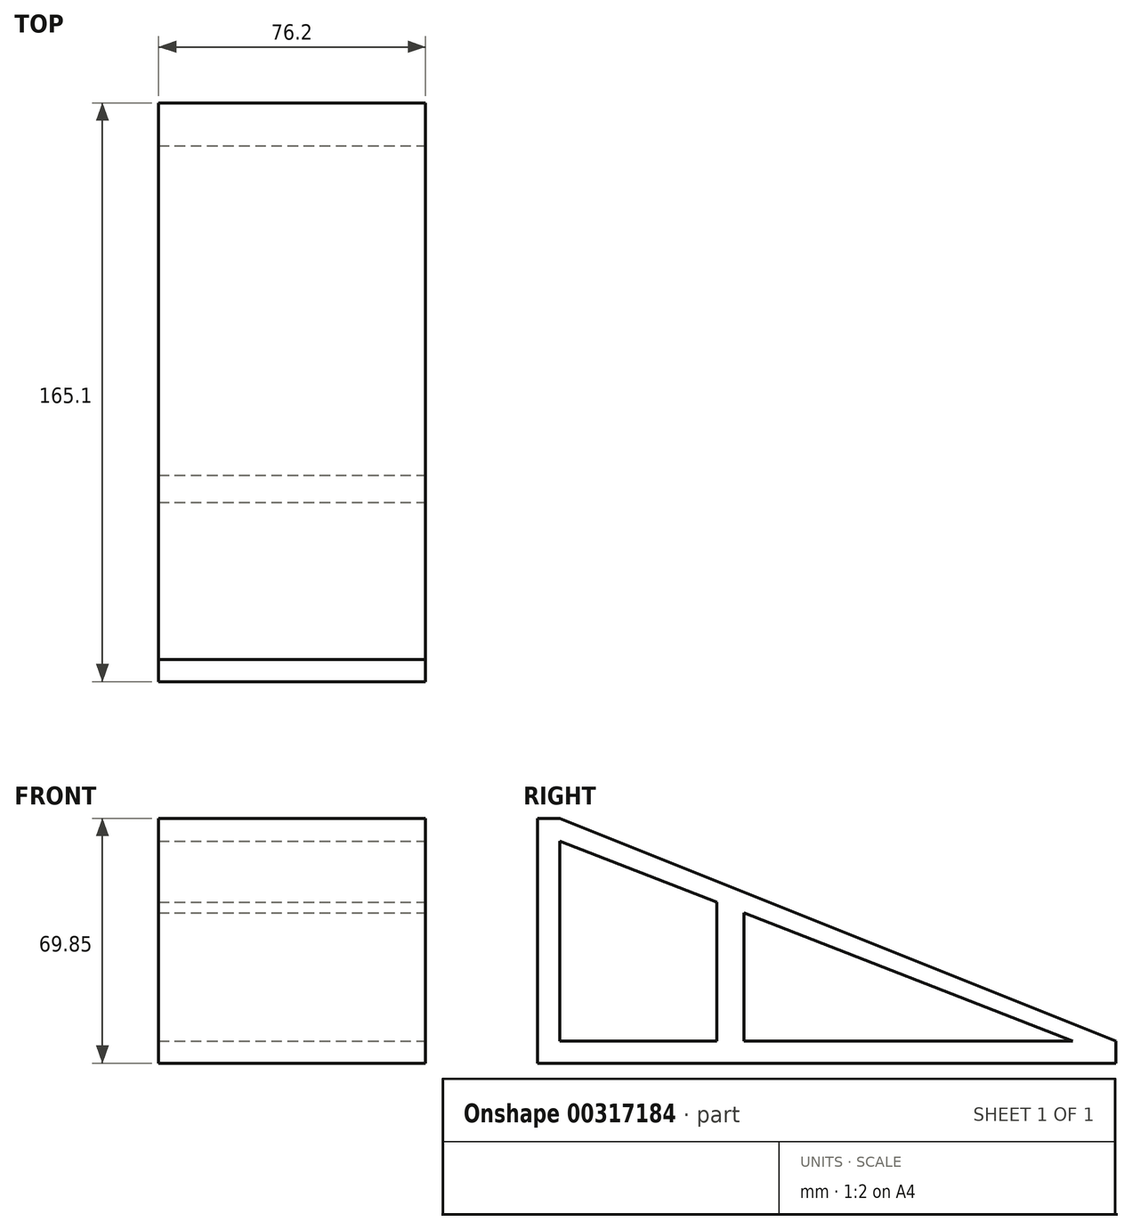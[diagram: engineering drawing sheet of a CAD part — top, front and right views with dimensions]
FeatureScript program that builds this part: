
annotation { "Feature Type Name" : "Feature", "Feature Type Description" : "" }
export const myFeature = defineFeature(function(context is Context, id is Id, definition is map)
    precondition{}
    {
        {
            var Q0;
            Q0=qCreatedBy(makeId("Right.planeOp"),FACE);
            var sketch = newSketch(context, id + "F0", { "sketchPlane" : qUnion([Q0])});
            skLineSegment(sketch, "E0.bottom", {"start": v(-82.55, 3.18) * mm, "end": v(82.55, 3.18) * mm});
            skLineSegment(sketch, "E0.top", {"start": v(-82.55, -3.18) * mm, "end": v(82.55, -3.18) * mm});
            skLineSegment(sketch, "E0.left", {"start": v(-82.55, 3.18) * mm, "end": v(-82.55, -3.18) * mm});
            skLineSegment(sketch, "E0.right", {"start": v(82.55, 3.18) * mm, "end": v(82.55, -3.18) * mm});
            skPoint(sketch, "E0.middle", {"position": v(0, 0) * mm});
            skLineSegment(sketch, "E1.bottom", {"start": v(-82.55, 3.18) * mm, "end": v(-76.2, 3.18) * mm});
            skLineSegment(sketch, "E1.top", {"start": v(-82.55, 66.68) * mm, "end": v(-76.2, 66.68) * mm});
            skLineSegment(sketch, "E1.left", {"start": v(-82.55, 3.18) * mm, "end": v(-82.55, 66.68) * mm});
            skLineSegment(sketch, "E1.right", {"start": v(-76.2, 3.18) * mm, "end": v(-76.2, 66.68) * mm});
            skLineSegment(sketch, "E2", {"start": v(-76.2, 66.68) * mm, "end": v(82.55, 3.18) * mm});
            skLineSegment(sketch, "E3", {"start": v(-76.2, 60.2) * mm, "end": v(70.25, 3.18) * mm});
            skLineSegment(sketch, "E4", {"start": v(-31.4, 3.18) * mm, "end": v(-31.4, 42.75) * mm});
            skLineSegment(sketch, "E5", {"start": v(-23.65, 3.18) * mm, "end": v(-23.65, 39.73) * mm});
            skSolve(sketch);
        }
        {
            var Q0;
            Q0 = qSketchRegion(id + "F0", true);
            var Q1;
            {var subQ0=sQuery(id+"F0.wireOp",EDGE,"E4");Q1=makeQuery(id+"F0.imprint","IMPRINT",FACE,{"disambiguationData":[TD([[makeQuery(id+"F0.imprint","IMPRINT",EDGE,{"derivedFrom":subQ0}),-1.0]])]});}
            extrude(context, id + "F1", {"entities" : qUnion([Q0, Q1]), "oppositeDirection" : true, "depth" : 76.2 * mm});
        }
    });
